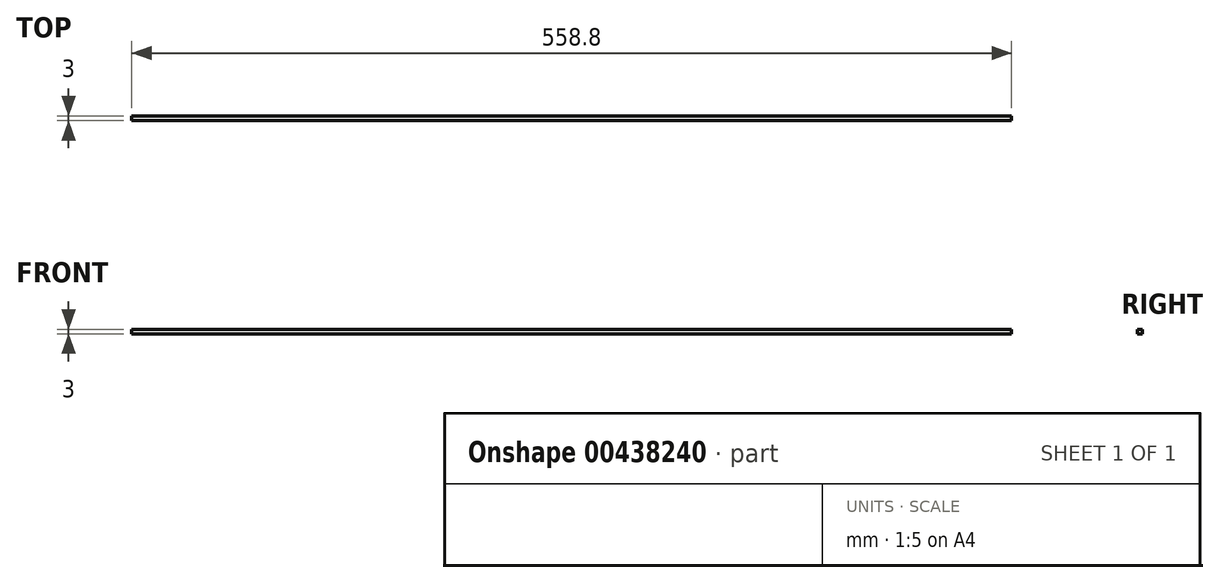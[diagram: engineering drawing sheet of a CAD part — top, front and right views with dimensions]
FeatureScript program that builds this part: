
annotation { "Feature Type Name" : "Feature", "Feature Type Description" : "" }
export const myFeature = defineFeature(function(context is Context, id is Id, definition is map)
    precondition{}
    {
        {
            var Q0;
            Q0=qCreatedBy(makeId("Front.planeOp"),FACE);
            var sketch = newSketch(context, id + "F0", { "sketchPlane" : qUnion([Q0])});
            skLineSegment(sketch, "E0.bottom", {"start": v(-272.65, 35.88) * mm, "end": v(286.15, 35.88) * mm});
            skLineSegment(sketch, "E0.top", {"start": v(-272.65, 38.88) * mm, "end": v(286.15, 38.88) * mm});
            skLineSegment(sketch, "E0.left", {"start": v(-272.65, 35.88) * mm, "end": v(-272.65, 38.88) * mm});
            skLineSegment(sketch, "E0.right", {"start": v(286.15, 35.88) * mm, "end": v(286.15, 38.88) * mm});
            skSolve(sketch);
        }
        {
            var Q0;
            Q0=makeQuery(id+"F0.imprint","IMPRINT",FACE,{"disambiguationData":[TD([[makeQuery(id+"F0.imprint","IMPRINT",EDGE,{"derivedFrom":sQuery(id+"F0.wireOp",EDGE,"E0.bottom")}),1.0]])]});
            extrude(context, id + "F1", {"entities" : qUnion([Q0]), "depth" : 3 * mm});
        }
    });
